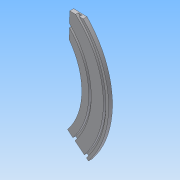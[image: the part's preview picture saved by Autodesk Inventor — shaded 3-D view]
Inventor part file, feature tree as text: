
AUTODESK INVENTOR PART (.ipt)
format: ipt  version: 2013 (Build 170138000, 138)  size: 158,720 bytes
history: native  units: in
note: dims shown in document units (in); Inventor stores cm internally (conversion verified against a paired STEP export)
features: extrude x2, plane x1, other x1, reference x1, sketch x1
ambient origin geometry x8: Origin, YZ Plane, XZ Plane, XY Plane, X Axis, Y Axis, Z Axis, Center Point
feature tree (6):
  plane  "Work Plane1"
  extrude  "Extrusion3"  Depth=2.5in
  extrude  "Extrusion4"  Depth=2.5in
  other  "ThermoBulbBorder"
  reference  "Reference2"
  sketch  "Sketch2"  dims[d0=24.0in d5=2.5in d6=2.5in d7=33.0in d8=0.32in d9=0.32in d10=2.25in d11=1.61in d12=6.0in d15=0.71in d16=0.0in d17=0.5in d19=0.48in d20=2.25in d21=0.5in d22=0.0in d23=0.5in d24=1.0in d25=0.48in]
